# Revit family: Safety & Protection_Bollard_UltiGroup_Steel Full Frame Bollard
name_source: partatom
category: Generic Models
revit_build: Autodesk Revit Architecture 2016 (Build: 20150220_1215(x64)
units: mm (PartAtom-declared; Revit-internal decimal feet)

## family parameters
Always vertical = Yes
Can host rebar = No
Cut with Voids When Loaded = No
Part Type = Normal
Room Calculation Point = No
Round Connector Dimension = Use Diameter
Shared = No
Work Plane-Based = No

## types (4) — shared parameters
Base Plate length = 250 mm  [stored 0.82021 ft]
Base Plate width = 250 mm  [stored 0.82021 ft]
Bollard radius = 83 mm
Bolt depth = 71 mm
Description = Galvanised Steel Full Frame Bollard
Fax = 07 846 2467
Galvanised Steel Yellow = Galvanised Steel Yellow
Plate Thickness = 12 mm  [stored 0.0393701 ft]
Send Message = http://ultigroup.co.nz
Type 1 Stays width = 750 mm
Type 2 Stays width = 1100 mm  [stored 3.60892 ft]
URL = www.ultigroup.co.nz
zero-valued in all types: InstallationGroup_ANZRS, ModifiedIssue_ANZRS

## per-type parameters (varying)
| type | Model | Opening Width | Opening height | Type 1 Stays | Type 2 Stays |
| Type 1 Full frame Bollard with Stays | Steel Full Frame Bollard - Type 1 with Stays | 2500 mm | 4200 mm | Yes | No |
| Type 2 Full Frame Bollard with Stays | Steel Full Frame Bollard - Type 2 with Stays | 2500 mm | 4200 mm | No | Yes |
| Type 3 Full Frame Bollard without Stays | Steel Full Frame Bollard - Type 3 without Stays | 3000 mm  [stored 9.84252 ft] | 4200 mm | No | No |
| Type 6 Full Frame Bollard with Stays | Steel Full Frame Bollard - Type 6 with stays | 4000 mm | 4500 mm | Yes | No |

note: [stored X ft] marks values corroborated as IEEE doubles in the binary element streams (Revit-internal decimal feet)

## geometry (parser evidence)
native form markers: Sweep x2
no freeform markers — native parametric forms only
